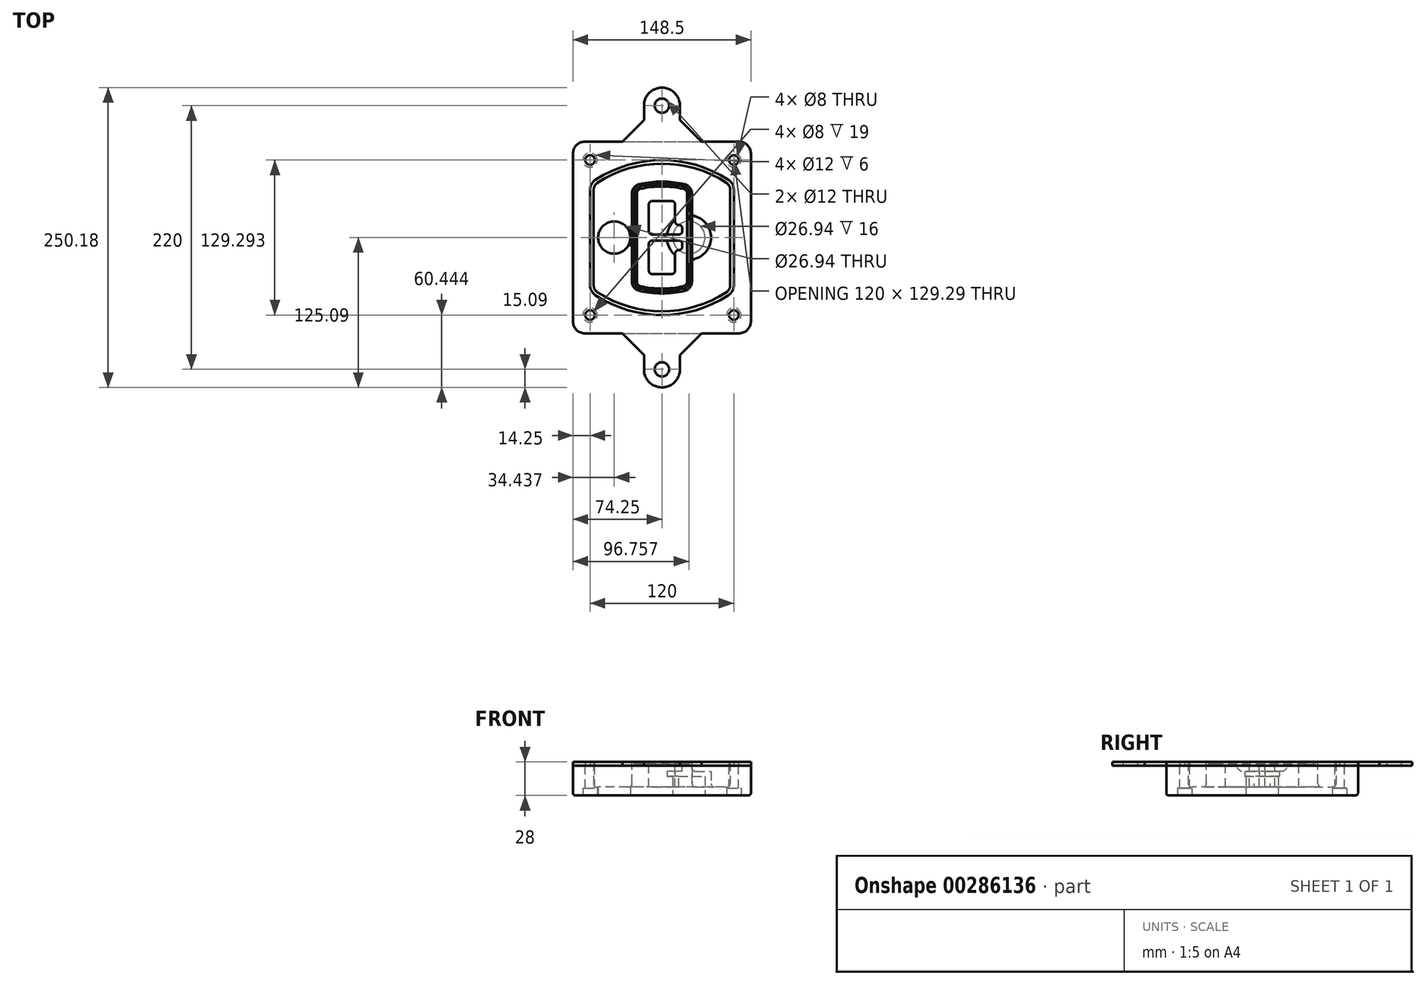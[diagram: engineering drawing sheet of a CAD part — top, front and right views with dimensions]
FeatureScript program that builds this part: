
annotation { "Feature Type Name" : "Feature", "Feature Type Description" : "" }
export const myFeature = defineFeature(function(context is Context, id is Id, definition is map)
    precondition{}
    {
        {
            var Q0;
            Q0=qCreatedBy(makeId("Top.planeOp"),FACE);
            var sketch = newSketch(context, id + "F0", { "sketchPlane" : qUnion([Q0])});
            skPoint(sketch, "E0.rect.middle", {"position": v(0, 0) * mm});
            skLineSegment(sketch, "E1.bottom", {"start": v(-64.25, -80) * mm, "end": v(64.25, -80) * mm});
            skLineSegment(sketch, "E1.top", {"start": v(-64.25, 80) * mm, "end": v(64.25, 80) * mm});
            skLineSegment(sketch, "E1.left", {"start": v(-74.25, -70) * mm, "end": v(-74.25, 70) * mm});
            skLineSegment(sketch, "E1.right", {"start": v(74.25, -70) * mm, "end": v(74.25, 70) * mm});
            skLineSegment(sketch, "E2", {"start": v(-74.25, 80) * mm, "end": v(74.25, -80) * mm, "construction": true});
            skLineSegment(sketch, "E3", {"start": v(74.25, 80) * mm, "end": v(-74.25, -80) * mm, "construction": true});
            skCircle(sketch, "E4", {"center": v(-60, 64.65) * mm, "radius": 4 * mm});
            skCircle(sketch, "E5", {"center": v(60, 64.65) * mm, "radius": 4 * mm});
            skCircle(sketch, "E6", {"center": v(60, -64.65) * mm, "radius": 4 * mm});
            skCircle(sketch, "E7", {"center": v(-60, -64.65) * mm, "radius": 4 * mm});
            skLineSegment(sketch, "E8", {"start": v(-60, 64.65) * mm, "end": v(60, 64.65) * mm, "construction": true});
            skLineSegment(sketch, "E9", {"start": v(60, 64.65) * mm, "end": v(60, -64.65) * mm, "construction": true});
            skLineSegment(sketch, "E10", {"start": v(60, -64.65) * mm, "end": v(-60, -64.65) * mm, "construction": true});
            skLineSegment(sketch, "E11", {"start": v(-60, -64.65) * mm, "end": v(-60, 64.65) * mm, "construction": true});
            skLineSegment(sketch, "E12", {"start": v(-60, 39.77) * mm, "end": v(-60, -39.77) * mm});
            skLineSegment(sketch, "E13", {"start": v(60, 39.77) * mm, "end": v(60, -39.77) * mm});
            skArc(sketch, "E14", {"start": v(55.47, 48.14) * mm, "mid": v(0, 64.65) * mm, "end": v(-55.47, 48.14) * mm});
            skArc(sketch, "E15", {"start": v(-55.47, -48.14) * mm, "mid": v(0, -64.65) * mm, "end": v(55.47, -48.14) * mm});
            skLineSegment(sketch, "E16", {"start": v(-60, 0) * mm, "end": v(60, 0) * mm, "construction": true});
            skPoint(sketch, "E17.visualSharp", {"position": v(-60, -45) * mm});
            skArc(sketch, "E17.filletArc", {"start": v(-60, -39.77) * mm, "mid": v(-58.8, -44.53) * mm, "end": v(-55.47, -48.14) * mm});
            skPoint(sketch, "E18.visualSharp", {"position": v(-60, 45) * mm});
            skArc(sketch, "E18.filletArc", {"start": v(-55.47, 48.14) * mm, "mid": v(-58.8, 44.53) * mm, "end": v(-60, 39.77) * mm});
            skPoint(sketch, "E19.visualSharp", {"position": v(60, 45) * mm});
            skArc(sketch, "E19.filletArc", {"start": v(60, 39.77) * mm, "mid": v(58.8, 44.53) * mm, "end": v(55.47, 48.14) * mm});
            skPoint(sketch, "E20.visualSharp", {"position": v(60, -45) * mm});
            skArc(sketch, "E20.filletArc", {"start": v(55.47, -48.14) * mm, "mid": v(58.8, -44.53) * mm, "end": v(60, -39.77) * mm});
            skPoint(sketch, "E21.visualSharp", {"position": v(-74.25, 80) * mm});
            skArc(sketch, "E21.filletArc", {"start": v(-64.25, 80) * mm, "mid": v(-71.32, 77.07) * mm, "end": v(-74.25, 70) * mm});
            skPoint(sketch, "E22.visualSharp", {"position": v(74.25, 80) * mm});
            skArc(sketch, "E22.filletArc", {"start": v(74.25, 70) * mm, "mid": v(71.32, 77.07) * mm, "end": v(64.25, 80) * mm});
            skPoint(sketch, "E23.visualSharp", {"position": v(74.25, -80) * mm});
            skArc(sketch, "E23.filletArc", {"start": v(64.25, -80) * mm, "mid": v(71.32, -77.07) * mm, "end": v(74.25, -70) * mm});
            skPoint(sketch, "E24.visualSharp", {"position": v(-74.25, -80) * mm});
            skArc(sketch, "E24.filletArc", {"start": v(-74.25, -70) * mm, "mid": v(-71.32, -77.07) * mm, "end": v(-64.25, -80) * mm});
            skArc(sketch, "E25.0", {"start": v(57, 39.77) * mm, "mid": v(56.16, 43.1) * mm, "end": v(53.83, 45.63) * mm});
            skLineSegment(sketch, "E25.1", {"start": v(57, 39.77) * mm, "end": v(57, -39.77) * mm});
            skArc(sketch, "E25.2", {"start": v(53.83, -45.63) * mm, "mid": v(56.16, -43.1) * mm, "end": v(57, -39.77) * mm});
            skArc(sketch, "E25.3", {"start": v(-53.83, -45.63) * mm, "mid": v(0, -61.65) * mm, "end": v(53.83, -45.63) * mm});
            skArc(sketch, "E25.4", {"start": v(-57, -39.77) * mm, "mid": v(-56.16, -43.1) * mm, "end": v(-53.83, -45.63) * mm});
            skArc(sketch, "E25.5", {"start": v(53.83, 45.63) * mm, "mid": v(0, 61.65) * mm, "end": v(-53.83, 45.63) * mm});
            skLineSegment(sketch, "E25.6", {"start": v(-57, 39.77) * mm, "end": v(-57, -39.77) * mm});
            skArc(sketch, "E25.7", {"start": v(-53.83, 45.63) * mm, "mid": v(-56.16, 43.1) * mm, "end": v(-57, 39.77) * mm});
            skArc(sketch, "E26.0", {"start": v(-57.66, 51.49) * mm, "mid": v(-62.31, 46.43) * mm, "end": v(-64, 39.77) * mm});
            skArc(sketch, "E26.1", {"start": v(57.66, 51.49) * mm, "mid": v(0, 68.65) * mm, "end": v(-57.66, 51.49) * mm});
            skArc(sketch, "E26.2", {"start": v(64, 39.77) * mm, "mid": v(62.31, 46.43) * mm, "end": v(57.66, 51.49) * mm});
            skLineSegment(sketch, "E26.3", {"start": v(64, 39.77) * mm, "end": v(64, -39.77) * mm});
            skArc(sketch, "E26.4", {"start": v(57.66, -51.49) * mm, "mid": v(62.31, -46.43) * mm, "end": v(64, -39.77) * mm});
            skLineSegment(sketch, "E26.5", {"start": v(-64, 39.77) * mm, "end": v(-64, -39.77) * mm});
            skArc(sketch, "E26.6", {"start": v(-57.66, -51.49) * mm, "mid": v(0, -68.65) * mm, "end": v(57.66, -51.49) * mm});
            skArc(sketch, "E26.7", {"start": v(-64, -39.77) * mm, "mid": v(-62.31, -46.43) * mm, "end": v(-57.66, -51.49) * mm});
            skSolve(sketch);
        }
        {
            var Q0;
            Q0=makeQuery(id+"F0.imprint","IMPRINT",FACE,{"disambiguationData":[TD([[makeQuery(id+"F0.imprint","IMPRINT",EDGE,{"derivedFrom":sQuery(id+"F0.wireOp",EDGE,"E1.bottom")}),1.0]])]});
            var Q1;
            Q1=makeQuery(id+"F0.imprint","IMPRINT",FACE,{"disambiguationData":[TD([[makeQuery(id+"F0.imprint","IMPRINT",EDGE,{"derivedFrom":sQuery(id+"F0.wireOp",EDGE,"E12")}),1.0]])]});
            var Q2;
            Q2=makeQuery(id+"F0.imprint","IMPRINT",FACE,{"disambiguationData":[TD([[makeQuery(id+"F0.imprint","IMPRINT",EDGE,{"derivedFrom":sQuery(id+"F0.wireOp",EDGE,"E25.0")}),1.0]])]});
            var Q3;
            Q3=makeQuery(id+"F0.imprint","IMPRINT",FACE,{"disambiguationData":[TD([[makeQuery(id+"F0.imprint","IMPRINT",EDGE,{"derivedFrom":sQuery(id+"F0.wireOp",EDGE,"E12")}),-1.0]])]});
            extrude(context, id + "F1", {"entities" : qUnion([Q0, Q1, Q2, Q3]), "oppositeDirection" : true, "depth" : 25 * mm});
        }
        {
            var Q0;
            Q0=makeQuery(id+"F0.imprint","IMPRINT",FACE,{"disambiguationData":[TD([[makeQuery(id+"F0.imprint","IMPRINT",EDGE,{"derivedFrom":sQuery(id+"F0.wireOp",EDGE,"E12")}),1.0]])]});
            extrude(context, id + "F2", {"entities" : qUnion([Q0]), "operationType" : NewBodyOperationType.ADD, "depth" : 3 * mm});
        }
        {
            var Q0;
            Q0=makeQuery(id+"F0.imprint","IMPRINT",FACE,{"disambiguationData":[TD([[makeQuery(id+"F0.imprint","IMPRINT",EDGE,{"derivedFrom":sQuery(id+"F0.wireOp",EDGE,"E25.0")}),1.0]])]});
            extrude(context, id + "F3", {"entities" : qUnion([Q0]), "operationType" : NewBodyOperationType.REMOVE, "oppositeDirection" : true, "depth" : 18 * mm});
        }
        {
            var Q0;
            Q0=makeQuery(id+"F2.opExtrude","CAP_FACE",FACE,{"disambiguationData":[OSD([sQuery(id+"F0.wireOp",EDGE,"E12"),sQuery(id+"F0.wireOp",EDGE,"E13"),sQuery(id+"F0.wireOp",EDGE,"E14"),sQuery(id+"F0.wireOp",EDGE,"E15"),sQuery(id+"F0.wireOp",EDGE,"E17.filletArc"),sQuery(id+"F0.wireOp",EDGE,"E18.filletArc"),sQuery(id+"F0.wireOp",EDGE,"E19.filletArc"),sQuery(id+"F0.wireOp",EDGE,"E20.filletArc"),sQuery(id+"F0.wireOp",EDGE,"E25.0"),sQuery(id+"F0.wireOp",EDGE,"E25.1"),sQuery(id+"F0.wireOp",EDGE,"E25.2"),sQuery(id+"F0.wireOp",EDGE,"E25.3"),sQuery(id+"F0.wireOp",EDGE,"E25.4"),sQuery(id+"F0.wireOp",EDGE,"E25.5"),sQuery(id+"F0.wireOp",EDGE,"E25.6"),sQuery(id+"F0.wireOp",EDGE,"E25.7")])],"isStart":false});
            var sketch = newSketch(context, id + "F4", { "sketchPlane" : qUnion([Q0])});
            skArc(sketch, "E27.0", {"start": v(-18.8, -44.5) * mm, "mid": v(0, -46.65) * mm, "end": v(18.8, -44.5) * mm});
            skArc(sketch, "E28.0", {"start": v(18.8, 44.5) * mm, "mid": v(0, 46.65) * mm, "end": v(-18.8, 44.5) * mm});
            skLineSegment(sketch, "E29", {"start": v(-25, 36.7) * mm, "end": v(-25, -36.7) * mm});
            skLineSegment(sketch, "E30", {"start": v(25, 36.7) * mm, "end": v(25, -36.7) * mm});
            skLineSegment(sketch, "E31", {"start": v(-25, 42.81) * mm, "end": v(25, 42.81) * mm, "construction": true});
            skLineSegment(sketch, "E32", {"start": v(-25, -42.81) * mm, "end": v(25, -42.81) * mm, "construction": true});
            skPoint(sketch, "E33.visualSharp", {"position": v(-25, 42.81) * mm});
            skArc(sketch, "E33.filletArc", {"start": v(-18.8, 44.5) * mm, "mid": v(-23.26, 41.69) * mm, "end": v(-25, 36.7) * mm});
            skPoint(sketch, "E34.visualSharp", {"position": v(25, 42.81) * mm});
            skArc(sketch, "E34.filletArc", {"start": v(25, 36.7) * mm, "mid": v(23.26, 41.69) * mm, "end": v(18.8, 44.5) * mm});
            skPoint(sketch, "E35.visualSharp", {"position": v(25, -42.81) * mm});
            skArc(sketch, "E35.filletArc", {"start": v(18.8, -44.5) * mm, "mid": v(23.26, -41.69) * mm, "end": v(25, -36.7) * mm});
            skPoint(sketch, "E36.visualSharp", {"position": v(-25, -42.81) * mm});
            skArc(sketch, "E36.filletArc", {"start": v(-25, -36.7) * mm, "mid": v(-23.26, -41.69) * mm, "end": v(-18.8, -44.5) * mm});
            skArc(sketch, "E37.0", {"start": v(53.83, 45.63) * mm, "mid": v(0, 61.65) * mm, "end": v(-53.83, 45.63) * mm});
            skArc(sketch, "E37.1", {"start": v(-53.83, 45.63) * mm, "mid": v(-56.16, 43.1) * mm, "end": v(-57, 39.77) * mm});
            skLineSegment(sketch, "E37.2", {"start": v(-57, 39.77) * mm, "end": v(-57, -39.77) * mm});
            skArc(sketch, "E37.3", {"start": v(-57, -39.77) * mm, "mid": v(-56.16, -43.1) * mm, "end": v(-53.83, -45.63) * mm});
            skArc(sketch, "E37.4", {"start": v(-53.83, -45.63) * mm, "mid": v(0, -61.65) * mm, "end": v(53.83, -45.63) * mm});
            skArc(sketch, "E37.5", {"start": v(53.83, -45.63) * mm, "mid": v(56.16, -43.1) * mm, "end": v(57, -39.77) * mm});
            skLineSegment(sketch, "E37.6", {"start": v(57, 39.77) * mm, "end": v(57, -39.77) * mm});
            skArc(sketch, "E37.7", {"start": v(57, 39.77) * mm, "mid": v(56.16, 43.1) * mm, "end": v(53.83, 45.63) * mm});
            skLineSegment(sketch, "E38.0", {"start": v(23, 36.7) * mm, "end": v(23, -36.7) * mm});
            skArc(sketch, "E38.1", {"start": v(18.35, -42.55) * mm, "mid": v(21.7, -40.44) * mm, "end": v(23, -36.7) * mm});
            skArc(sketch, "E38.2", {"start": v(-18.35, -42.55) * mm, "mid": v(0, -44.65) * mm, "end": v(18.35, -42.55) * mm});
            skArc(sketch, "E38.3", {"start": v(-23, -36.7) * mm, "mid": v(-21.7, -40.44) * mm, "end": v(-18.35, -42.55) * mm});
            skLineSegment(sketch, "E38.4", {"start": v(-23, 36.7) * mm, "end": v(-23, -36.7) * mm});
            skArc(sketch, "E38.5", {"start": v(23, 36.7) * mm, "mid": v(21.7, 40.44) * mm, "end": v(18.35, 42.55) * mm});
            skArc(sketch, "E38.6", {"start": v(-18.35, 42.55) * mm, "mid": v(-21.7, 40.44) * mm, "end": v(-23, 36.7) * mm});
            skArc(sketch, "E38.7", {"start": v(18.35, 42.55) * mm, "mid": v(0, 44.65) * mm, "end": v(-18.35, 42.55) * mm});
            skArc(sketch, "E39.0", {"start": v(21, 36.7) * mm, "mid": v(20.13, 39.2) * mm, "end": v(17.9, 40.6) * mm});
            skLineSegment(sketch, "E39.1", {"start": v(21, 36.7) * mm, "end": v(21, -36.7) * mm});
            skArc(sketch, "E39.2", {"start": v(17.9, -40.6) * mm, "mid": v(20.13, -39.2) * mm, "end": v(21, -36.7) * mm});
            skArc(sketch, "E39.3", {"start": v(-17.9, -40.6) * mm, "mid": v(0, -42.65) * mm, "end": v(17.9, -40.6) * mm});
            skArc(sketch, "E39.4", {"start": v(-21, -36.7) * mm, "mid": v(-20.13, -39.2) * mm, "end": v(-17.9, -40.6) * mm});
            skArc(sketch, "E39.5", {"start": v(17.9, 40.6) * mm, "mid": v(0, 42.65) * mm, "end": v(-17.9, 40.6) * mm});
            skLineSegment(sketch, "E39.6", {"start": v(-21, 36.7) * mm, "end": v(-21, -36.7) * mm});
            skArc(sketch, "E39.7", {"start": v(-17.9, 40.6) * mm, "mid": v(-20.13, 39.2) * mm, "end": v(-21, 36.7) * mm});
            skLineSegment(sketch, "E40", {"start": v(-25, 0) * mm, "end": v(25, 0) * mm, "construction": true});
            skLineSegment(sketch, "E41", {"start": v(-11, 5.5) * mm, "end": v(-11, 27.5) * mm});
            skLineSegment(sketch, "E42", {"start": v(-8, 30.5) * mm, "end": v(8, 30.5) * mm});
            skLineSegment(sketch, "E43", {"start": v(11, 27.5) * mm, "end": v(11, 13.5) * mm});
            skLineSegment(sketch, "E44", {"start": v(14, 10.5) * mm, "end": v(14, 10.5) * mm});
            skLineSegment(sketch, "E45", {"start": v(17, 7.5) * mm, "end": v(17, 5.5) * mm});
            skLineSegment(sketch, "E46", {"start": v(14, 2.5) * mm, "end": v(-8, 2.5) * mm});
            skPoint(sketch, "E47.visualSharp", {"position": v(-11, 30.5) * mm});
            skArc(sketch, "E47.filletArc", {"start": v(-8, 30.5) * mm, "mid": v(-10.12, 29.62) * mm, "end": v(-11, 27.5) * mm});
            skPoint(sketch, "E48.visualSharp", {"position": v(11, 30.5) * mm});
            skArc(sketch, "E48.filletArc", {"start": v(11, 27.5) * mm, "mid": v(10.12, 29.62) * mm, "end": v(8, 30.5) * mm});
            skPoint(sketch, "E49.visualSharp", {"position": v(11, 10.5) * mm});
            skArc(sketch, "E49.filletArc", {"start": v(11, 13.5) * mm, "mid": v(11.88, 11.38) * mm, "end": v(14, 10.5) * mm});
            skPoint(sketch, "E50.visualSharp", {"position": v(17, 10.5) * mm});
            skArc(sketch, "E50.filletArc", {"start": v(17, 7.5) * mm, "mid": v(16.12, 9.62) * mm, "end": v(14, 10.5) * mm});
            skPoint(sketch, "E51.visualSharp", {"position": v(17, 2.5) * mm});
            skArc(sketch, "E51.filletArc", {"start": v(14, 2.5) * mm, "mid": v(16.12, 3.38) * mm, "end": v(17, 5.5) * mm});
            skPoint(sketch, "E52.visualSharp", {"position": v(-11, 2.5) * mm});
            skArc(sketch, "E52.filletArc", {"start": v(-11, 5.5) * mm, "mid": v(-10.12, 3.38) * mm, "end": v(-8, 2.5) * mm});
            skLineSegment(sketch, "E53.0.MirrorCS", {"start": v(14, -2.5) * mm, "end": v(-8, -2.5) * mm});
            skArc(sketch, "E54.0.MirrorCS", {"start": v(-11, -5.5) * mm, "mid": v(-10.12, -3.38) * mm, "end": v(-8, -2.5) * mm});
            skLineSegment(sketch, "E55.0.MirrorCS", {"start": v(-11, -5.5) * mm, "end": v(-11, -27.5) * mm});
            skArc(sketch, "E56.0.MirrorCS", {"start": v(-8, -30.5) * mm, "mid": v(-10.12, -29.62) * mm, "end": v(-11, -27.5) * mm});
            skLineSegment(sketch, "E57.0.MirrorCS", {"start": v(-8, -30.5) * mm, "end": v(8, -30.5) * mm});
            skArc(sketch, "E58.0.MirrorCS", {"start": v(11, -27.5) * mm, "mid": v(10.12, -29.62) * mm, "end": v(8, -30.5) * mm});
            skLineSegment(sketch, "E59.0.MirrorCS", {"start": v(11, -27.5) * mm, "end": v(11, -13.5) * mm});
            skArc(sketch, "E60.0.MirrorCS", {"start": v(11, -13.5) * mm, "mid": v(11.88, -11.38) * mm, "end": v(14, -10.5) * mm});
            skArc(sketch, "E61.0.MirrorCS", {"start": v(17, -7.5) * mm, "mid": v(16.12, -9.62) * mm, "end": v(14, -10.5) * mm});
            skLineSegment(sketch, "E62.0.MirrorCS", {"start": v(17, -7.5) * mm, "end": v(17, -5.5) * mm});
            skArc(sketch, "E63.0.MirrorCS", {"start": v(14, -2.5) * mm, "mid": v(16.12, -3.38) * mm, "end": v(17, -5.5) * mm});
            skSolve(sketch);
        }
        {
            var Q0;
            Q0=makeQuery(id+"F4.imprint","IMPRINT",FACE,{"disambiguationData":[TD([[makeQuery(id+"F4.imprint","IMPRINT",EDGE,{"derivedFrom":sQuery(id+"F4.wireOp",EDGE,"E27.0")}),1.0]])]});
            var Q1;
            Q1=makeQuery(id+"F4.imprint","IMPRINT",FACE,{"disambiguationData":[TD([[makeQuery(id+"F4.imprint","IMPRINT",EDGE,{"derivedFrom":sQuery(id+"F4.wireOp",EDGE,"E38.0")}),-1.0]])]});
            var Q2;
            Q2=makeQuery(id+"F4.imprint","IMPRINT",FACE,{"disambiguationData":[TD([[makeQuery(id+"F4.imprint","IMPRINT",EDGE,{"derivedFrom":sQuery(id+"F4.wireOp",EDGE,"E39.0")}),1.0]])]});
            extrude(context, id + "F5", {"entities" : qUnion([Q0, Q1, Q2]), "operationType" : NewBodyOperationType.ADD, "endBound" : BoundingType.UP_TO_NEXT, "oppositeDirection" : true, "depth" : 25 * mm});
        }
        {
            var Q0;
            Q0=makeQuery(id+"F4.imprint","IMPRINT",FACE,{"disambiguationData":[TD([[makeQuery(id+"F4.imprint","IMPRINT",EDGE,{"derivedFrom":sQuery(id+"F4.wireOp",EDGE,"E38.0")}),-1.0]])]});
            extrude(context, id + "F6", {"entities" : qUnion([Q0]), "operationType" : NewBodyOperationType.REMOVE, "oppositeDirection" : true, "depth" : 2 * mm});
        }
        {
            var Q0;
            Q0=makeQuery(id+"F1.opExtrude","CAP_FACE",FACE,{"disambiguationData":[OSD([sQuery(id+"F0.wireOp",EDGE,"E1.bottom"),sQuery(id+"F0.wireOp",EDGE,"E1.top"),sQuery(id+"F0.wireOp",EDGE,"E1.left"),sQuery(id+"F0.wireOp",EDGE,"E1.right"),sQuery(id+"F0.wireOp",EDGE,"E4"),sQuery(id+"F0.wireOp",EDGE,"E5"),sQuery(id+"F0.wireOp",EDGE,"E6"),sQuery(id+"F0.wireOp",EDGE,"E7"),sQuery(id+"F0.wireOp",EDGE,"E21.filletArc"),sQuery(id+"F0.wireOp",EDGE,"E22.filletArc"),sQuery(id+"F0.wireOp",EDGE,"E23.filletArc"),sQuery(id+"F0.wireOp",EDGE,"E24.filletArc")])],"isStart":false});
            var sketch = newSketch(context, id + "F7", { "sketchPlane" : qUnion([Q0])});
            skCircle(sketch, "E64", {"center": v(22.5, 0) * mm, "radius": 13.47 * mm});
            skCircle(sketch, "E65", {"center": v(-39.81, 0) * mm, "radius": 13.47 * mm});
            skLineSegment(sketch, "E66", {"start": v(74.25, 0) * mm, "end": v(-74.25, 0) * mm});
            skCircle(sketch, "E67", {"center": v(22.5, 0) * mm, "radius": 18.47 * mm});
            skCircle(sketch, "E68", {"center": v(60, -64.65) * mm, "radius": 6 * mm});
            skCircle(sketch, "E69", {"center": v(-60, -64.65) * mm, "radius": 6 * mm});
            skCircle(sketch, "E70", {"center": v(-60, 64.65) * mm, "radius": 6 * mm});
            skCircle(sketch, "E71", {"center": v(60, 64.65) * mm, "radius": 6 * mm});
            skSolve(sketch);
        }
        {
            var Q0;
            {var subQ1=sQuery(id+"F7.wireOp",EDGE,"E66");var subQ4=sQuery(id+"F7.wireOp",EDGE,"E64");var subQ6=makeQuery(id+"F7.imprint","INTERSECT",VERTEX,{"disambiguationData":[OD(0.0)],"derivedFrom":[subQ4,subQ1]});Q0=makeQuery(id+"F7.imprint","IMPRINT",FACE,{"disambiguationData":[TD([[makeQuery(id+"F7.imprint","IMPRINT",EDGE,{"disambiguationData":[TD([[subQ6,-1.0]])],"derivedFrom":subQ4}),-1.0]])]});}
            var Q1;
            {var subQ0=sQuery(id+"F7.wireOp",EDGE,"E66");var subQ1=sQuery(id+"F7.wireOp",EDGE,"E64");var subQ3=makeQuery(id+"F7.imprint","INTERSECT",VERTEX,{"disambiguationData":[OD(0.0)],"derivedFrom":[subQ1,subQ0]});Q1=makeQuery(id+"F7.imprint","IMPRINT",FACE,{"disambiguationData":[TD([[makeQuery(id+"F7.imprint","IMPRINT",EDGE,{"disambiguationData":[TD([[subQ3,-1.0]])],"derivedFrom":subQ1}),1.0]])]});}
            var Q2;
            {var subQ0=sQuery(id+"F7.wireOp",EDGE,"E66");var subQ1=sQuery(id+"F7.wireOp",EDGE,"E64");var subQ3=makeQuery(id+"F7.imprint","INTERSECT",VERTEX,{"disambiguationData":[OD(0.0)],"derivedFrom":[subQ1,subQ0]});Q2=makeQuery(id+"F7.imprint","IMPRINT",FACE,{"disambiguationData":[TD([[makeQuery(id+"F7.imprint","IMPRINT",EDGE,{"disambiguationData":[TD([[subQ3,1.0]])],"derivedFrom":subQ1}),1.0]])]});}
            var Q3;
            {var subQ1=sQuery(id+"F7.wireOp",EDGE,"E66");var subQ4=sQuery(id+"F7.wireOp",EDGE,"E64");var subQ6=makeQuery(id+"F7.imprint","INTERSECT",VERTEX,{"disambiguationData":[OD(0.0)],"derivedFrom":[subQ4,subQ1]});Q3=makeQuery(id+"F7.imprint","IMPRINT",FACE,{"disambiguationData":[TD([[makeQuery(id+"F7.imprint","IMPRINT",EDGE,{"disambiguationData":[TD([[subQ6,1.0]])],"derivedFrom":subQ4}),-1.0]])]});}
            extrude(context, id + "F8", {"entities" : qUnion([Q0, Q1, Q2, Q3]), "operationType" : NewBodyOperationType.ADD, "oppositeDirection" : true, "depth" : 20 * mm});
        }
        {
            var Q0;
            {var subQ0=sQuery(id+"F7.wireOp",EDGE,"E66");var subQ1=sQuery(id+"F7.wireOp",EDGE,"E64");var subQ3=makeQuery(id+"F7.imprint","INTERSECT",VERTEX,{"disambiguationData":[OD(0.0)],"derivedFrom":[subQ1,subQ0]});Q0=makeQuery(id+"F7.imprint","IMPRINT",FACE,{"disambiguationData":[TD([[makeQuery(id+"F7.imprint","IMPRINT",EDGE,{"disambiguationData":[TD([[subQ3,-1.0]])],"derivedFrom":subQ1}),1.0]])]});}
            var Q1;
            {var subQ0=sQuery(id+"F7.wireOp",EDGE,"E66");var subQ1=sQuery(id+"F7.wireOp",EDGE,"E64");var subQ3=makeQuery(id+"F7.imprint","INTERSECT",VERTEX,{"disambiguationData":[OD(0.0)],"derivedFrom":[subQ1,subQ0]});Q1=makeQuery(id+"F7.imprint","IMPRINT",FACE,{"disambiguationData":[TD([[makeQuery(id+"F7.imprint","IMPRINT",EDGE,{"disambiguationData":[TD([[subQ3,1.0]])],"derivedFrom":subQ1}),1.0]])]});}
            extrude(context, id + "F9", {"entities" : qUnion([Q0, Q1]), "operationType" : NewBodyOperationType.REMOVE, "oppositeDirection" : true, "depth" : 16 * mm});
        }
        {
            var Q0;
            {var subQ0=sQuery(id+"F7.wireOp",EDGE,"E66");var subQ1=sQuery(id+"F7.wireOp",EDGE,"E65");var subQ3=makeQuery(id+"F7.imprint","INTERSECT",VERTEX,{"disambiguationData":[OD(0.0)],"derivedFrom":[subQ1,subQ0]});Q0=makeQuery(id+"F7.imprint","IMPRINT",FACE,{"disambiguationData":[TD([[makeQuery(id+"F7.imprint","IMPRINT",EDGE,{"disambiguationData":[TD([[subQ3,-1.0]])],"derivedFrom":subQ1}),1.0]])]});}
            var Q1;
            {var subQ0=sQuery(id+"F7.wireOp",EDGE,"E66");var subQ1=sQuery(id+"F7.wireOp",EDGE,"E65");var subQ3=makeQuery(id+"F7.imprint","INTERSECT",VERTEX,{"disambiguationData":[OD(0.0)],"derivedFrom":[subQ1,subQ0]});Q1=makeQuery(id+"F7.imprint","IMPRINT",FACE,{"disambiguationData":[TD([[makeQuery(id+"F7.imprint","IMPRINT",EDGE,{"disambiguationData":[TD([[subQ3,1.0]])],"derivedFrom":subQ1}),1.0]])]});}
            extrude(context, id + "F10", {"entities" : qUnion([Q0, Q1]), "operationType" : NewBodyOperationType.REMOVE, "oppositeDirection" : true, "depth" : 25 * mm});
        }
        {
            var Q0;
            Q0=makeQuery(id+"F7.imprint","IMPRINT",FACE,{"disambiguationData":[TD([[makeQuery(id+"F7.imprint","IMPRINT",EDGE,{"derivedFrom":sQuery(id+"F7.wireOp",EDGE,"E68")}),1.0]])]});
            var Q1;
            Q1=makeQuery(id+"F7.imprint","IMPRINT",FACE,{"disambiguationData":[TD([[makeQuery(id+"F7.imprint","IMPRINT",EDGE,{"derivedFrom":makeQuery(id+"F1.opExtrude","CAP_EDGE",EDGE,{"disambiguationData":[OSD([sQuery(id+"F0.wireOp",EDGE,"E5")])],"isStart":false})}),-1.0]])]});
            var Q2;
            Q2=makeQuery(id+"F7.imprint","IMPRINT",FACE,{"disambiguationData":[TD([[makeQuery(id+"F7.imprint","IMPRINT",EDGE,{"derivedFrom":sQuery(id+"F7.wireOp",EDGE,"E69")}),1.0]])]});
            var Q3;
            Q3=makeQuery(id+"F7.imprint","IMPRINT",FACE,{"disambiguationData":[TD([[makeQuery(id+"F7.imprint","IMPRINT",EDGE,{"derivedFrom":makeQuery(id+"F1.opExtrude","CAP_EDGE",EDGE,{"disambiguationData":[OSD([sQuery(id+"F0.wireOp",EDGE,"E4")])],"isStart":false})}),-1.0]])]});
            var Q4;
            Q4=makeQuery(id+"F7.imprint","IMPRINT",FACE,{"disambiguationData":[TD([[makeQuery(id+"F7.imprint","IMPRINT",EDGE,{"derivedFrom":sQuery(id+"F7.wireOp",EDGE,"E70")}),1.0]])]});
            var Q5;
            Q5=makeQuery(id+"F7.imprint","IMPRINT",FACE,{"disambiguationData":[TD([[makeQuery(id+"F7.imprint","IMPRINT",EDGE,{"derivedFrom":makeQuery(id+"F1.opExtrude","CAP_EDGE",EDGE,{"disambiguationData":[OSD([sQuery(id+"F0.wireOp",EDGE,"E7")])],"isStart":false})}),-1.0]])]});
            var Q6;
            Q6=makeQuery(id+"F7.imprint","IMPRINT",FACE,{"disambiguationData":[TD([[makeQuery(id+"F7.imprint","IMPRINT",EDGE,{"derivedFrom":sQuery(id+"F7.wireOp",EDGE,"E71")}),1.0]])]});
            var Q7;
            Q7=makeQuery(id+"F7.imprint","IMPRINT",FACE,{"disambiguationData":[TD([[makeQuery(id+"F7.imprint","IMPRINT",EDGE,{"derivedFrom":makeQuery(id+"F1.opExtrude","CAP_EDGE",EDGE,{"disambiguationData":[OSD([sQuery(id+"F0.wireOp",EDGE,"E6")])],"isStart":false})}),-1.0]])]});
            extrude(context, id + "F11", {"entities" : qUnion([Q0, Q1, Q2, Q3, Q4, Q5, Q6, Q7]), "operationType" : NewBodyOperationType.REMOVE, "oppositeDirection" : true, "depth" : 6 * mm});
        }
        {
            var Q0;
            Q0=makeQuery(id+"F9.boolean.opBoolean","COPY",FACE,{"derivedFrom":makeQuery(id+"F9.opExtrude","CAP_FACE",FACE,{"disambiguationData":[OSD([sQuery(id+"F7.wireOp",EDGE,"E64")])],"isStart":false})});
            var sketch = newSketch(context, id + "F12", { "sketchPlane" : qUnion([Q0])});
            skArc(sketch, "E72.0", {"start": v(11, 14.45) * mm, "mid": v(6.45, 9.13) * mm, "end": v(4.2, 2.5) * mm});
            skArc(sketch, "E72.1", {"start": v(4.2, -2.5) * mm, "mid": v(6.45, -9.13) * mm, "end": v(11, -14.45) * mm});
            skLineSegment(sketch, "E73", {"start": v(4.2, -2.5) * mm, "end": v(14, -2.5) * mm});
            skLineSegment(sketch, "E74.0", {"start": v(14, 2.5) * mm, "end": v(4.2, 2.5) * mm});
            skArc(sketch, "E74.1", {"start": v(14, 2.5) * mm, "mid": v(16.12, 3.38) * mm, "end": v(17, 5.5) * mm});
            skLineSegment(sketch, "E74.2", {"start": v(17, 7.5) * mm, "end": v(17, 5.5) * mm});
            skArc(sketch, "E74.3", {"start": v(17, 7.5) * mm, "mid": v(16.12, 9.62) * mm, "end": v(14, 10.5) * mm});
            skArc(sketch, "E74.4", {"start": v(11, 13.5) * mm, "mid": v(11.88, 11.38) * mm, "end": v(14, 10.5) * mm});
            skLineSegment(sketch, "E74.5", {"start": v(11, 14.45) * mm, "end": v(11, 13.5) * mm});
            skLineSegment(sketch, "E74.7", {"start": v(14, -2.5) * mm, "end": v(4.2, -2.5) * mm});
            skArc(sketch, "E74.8", {"start": v(14, -2.5) * mm, "mid": v(16.12, -3.38) * mm, "end": v(17, -5.5) * mm});
            skLineSegment(sketch, "E74.9", {"start": v(17, -7.5) * mm, "end": v(17, -5.5) * mm});
            skArc(sketch, "E74.10", {"start": v(17, -7.5) * mm, "mid": v(16.12, -9.62) * mm, "end": v(14, -10.5) * mm});
            skArc(sketch, "E74.11", {"start": v(11, -13.5) * mm, "mid": v(11.88, -11.38) * mm, "end": v(14, -10.5) * mm});
            skLineSegment(sketch, "E74.12", {"start": v(11, -14.45) * mm, "end": v(11, -13.5) * mm});
            skPoint(sketch, "E75.orphan", {"position": v(11, -27.5) * mm});
            skPoint(sketch, "E76.orphan", {"position": v(-8, -2.5) * mm});
            skPoint(sketch, "E77.orphan", {"position": v(-8, 2.5) * mm});
            skPoint(sketch, "E78.orphan", {"position": v(11, 27.5) * mm});
            skSolve(sketch);
        }
        {
            var Q0;
            {var subQ7=sQuery(id+"F12.wireOp",EDGE,"E72.0");var subQ14=sQuery(id+"F12.wireOp",EDGE,"E72.1");var subQ16=sQuery(id+"F12.wireOp",EDGE,"E74.1");var subQ18=sQuery(id+"F12.wireOp",EDGE,"E74.8");Q0=qUnion([makeQuery(id+"F12.imprint","IMPRINT",FACE,{"disambiguationData":[TD([[makeQuery(id+"F12.imprint","IMPRINT",EDGE,{"derivedFrom":subQ7}),1.0]])]}),makeQuery(id+"F12.imprint","IMPRINT",FACE,{"disambiguationData":[TD([[makeQuery(id+"F12.imprint","IMPRINT",EDGE,{"derivedFrom":subQ14}),1.0]])]}),makeQuery(id+"F12.imprint","IMPRINT",FACE,{"disambiguationData":[TD([[makeQuery(id+"F12.imprint","IMPRINT",EDGE,{"derivedFrom":subQ16}),1.0]])]}),makeQuery(id+"F12.imprint","IMPRINT",FACE,{"disambiguationData":[TD([[makeQuery(id+"F12.imprint","IMPRINT",EDGE,{"derivedFrom":subQ18}),-1.0]])]})]);}
            var Q1;
            Q1=makeQuery(id+"F5.boolean.opBoolean","SPLIT",FACE,{"disambiguationData":[TD([makeQuery(id+"F5.opExtrude","SWEPT_FACE",FACE,{"disambiguationData":[OSD([sQuery(id+"F4.wireOp",EDGE,"E41")])]})])],"derivedFrom":makeQuery(id+"F3.boolean.opBoolean","COPY",FACE,{"derivedFrom":makeQuery(id+"F3.opExtrude","CAP_FACE",FACE,{"disambiguationData":[OSD([sQuery(id+"F0.wireOp",EDGE,"E25.0"),sQuery(id+"F0.wireOp",EDGE,"E25.1"),sQuery(id+"F0.wireOp",EDGE,"E25.2"),sQuery(id+"F0.wireOp",EDGE,"E25.3"),sQuery(id+"F0.wireOp",EDGE,"E25.4"),sQuery(id+"F0.wireOp",EDGE,"E25.5"),sQuery(id+"F0.wireOp",EDGE,"E25.6"),sQuery(id+"F0.wireOp",EDGE,"E25.7")])],"isStart":false})})});
            extrude(context, id + "F13", {"entities" : qUnion([Q0]), "operationType" : NewBodyOperationType.REMOVE, "endBound" : BoundingType.UP_TO_SURFACE, "endBoundEntityFace" : qUnion([Q1]), "depth" : 25 * mm});
        }
        {
            var Q0;
            Q0=makeQuery(id+"F3.boolean.opBoolean","COPY",EDGE,{"derivedFrom":makeQuery(id+"F3.opExtrude","CAP_EDGE",EDGE,{"disambiguationData":[OSD([sQuery(id+"F0.wireOp",EDGE,"E25.6")])],"isStart":false})});
            var Q1;
            Q1=makeQuery(id+"F8.boolean.opBoolean","INTERSECT",EDGE,{"derivedFrom":[makeQuery(id+"F5.opExtrude","SWEPT_FACE",FACE,{"disambiguationData":[OSD([sQuery(id+"F4.wireOp",EDGE,"E30")])]}),makeQuery(id+"F8.opExtrude","CAP_FACE",FACE,{"disambiguationData":[OSD([sQuery(id+"F7.wireOp",EDGE,"E67")])],"isStart":false})]});
            var Q2;
            Q2=makeQuery(id+"F8.boolean.opBoolean","INTERSECT",EDGE,{"disambiguationData":[OD(1.0)],"derivedFrom":[makeQuery(id+"F5.opExtrude","SWEPT_FACE",FACE,{"disambiguationData":[OSD([sQuery(id+"F4.wireOp",EDGE,"E30")])]}),makeQuery(id+"F8.opExtrude","SWEPT_FACE",FACE,{"disambiguationData":[OSD([sQuery(id+"F7.wireOp",EDGE,"E67")])]})]});
            var Q3;
            {var subQ0=sQuery(id+"F4.wireOp",EDGE,"E30");Q3=makeQuery(id+"F8.boolean.opBoolean","SPLIT",EDGE,{"disambiguationData":[TD([makeQuery(id+"F5.opExtrude","SWEPT_FACE",FACE,{"disambiguationData":[OSD([sQuery(id+"F4.wireOp",EDGE,"E35.filletArc")])]})])],"derivedFrom":makeQuery(id+"F5.opExtrude","CAP_EDGE",EDGE,{"disambiguationData":[OSD([subQ0])],"isStart":false})});}
            var Q4;
            {var subQ0=sQuery(id+"F0.wireOp",EDGE,"E25.7");var subQ1=sQuery(id+"F0.wireOp",EDGE,"E25.1");var subQ2=sQuery(id+"F0.wireOp",EDGE,"E25.6");var subQ3=sQuery(id+"F0.wireOp",EDGE,"E25.5");var subQ4=sQuery(id+"F0.wireOp",EDGE,"E25.4");var subQ5=sQuery(id+"F0.wireOp",EDGE,"E25.0");var subQ6=sQuery(id+"F0.wireOp",EDGE,"E25.2");var subQ7=sQuery(id+"F0.wireOp",EDGE,"E25.3");Q4=makeQuery(id+"F8.boolean.opBoolean","INTERSECT",EDGE,{"derivedFrom":[makeQuery(id+"F5.boolean.opBoolean","SPLIT",FACE,{"disambiguationData":[TD([makeQuery(id+"F2.opExtrude","SWEPT_FACE",FACE,{"disambiguationData":[OSD([subQ5])]})])],"derivedFrom":makeQuery(id+"F3.boolean.opBoolean","COPY",FACE,{"derivedFrom":makeQuery(id+"F3.opExtrude","CAP_FACE",FACE,{"disambiguationData":[OSD([subQ5,subQ1,subQ6,subQ7,subQ4,subQ3,subQ2,subQ0])],"isStart":false})})}),makeQuery(id+"F8.opExtrude","SWEPT_FACE",FACE,{"disambiguationData":[OSD([sQuery(id+"F7.wireOp",EDGE,"E67")])]})]});}
            var Q5;
            Q5=makeQuery(id+"F8.boolean.opBoolean","INTERSECT",EDGE,{"disambiguationData":[OD(0.0)],"derivedFrom":[makeQuery(id+"F5.opExtrude","SWEPT_FACE",FACE,{"disambiguationData":[OSD([sQuery(id+"F4.wireOp",EDGE,"E30")])]}),makeQuery(id+"F8.opExtrude","SWEPT_FACE",FACE,{"disambiguationData":[OSD([sQuery(id+"F7.wireOp",EDGE,"E67")])]})]});
            fillet(context, id + "F14", {"entities" : qUnion([Q0, Q1, Q2, Q3, Q4, Q5]), "radius" : 3 * mm, "tangentPropagation" : true, "allowEdgeOverflow" : false});
        }
        {
            var Q0;
            Q0=makeQuery(id+"F1.opExtrude","CAP_EDGE",EDGE,{"disambiguationData":[OSD([sQuery(id+"F0.wireOp",EDGE,"E1.bottom")])],"isStart":false});
            fillet(context, id + "F15", {"entities" : qUnion([Q0]), "radius" : 2 * mm, "tangentPropagation" : true, "allowEdgeOverflow" : false});
        }
        {
            var Q0;
            {var subQ0=sQuery(id+"F0.wireOp",EDGE,"E21.filletArc");var subQ1=sQuery(id+"F0.wireOp",EDGE,"E7");var subQ2=sQuery(id+"F0.wireOp",EDGE,"E6");var subQ3=sQuery(id+"F0.wireOp",EDGE,"E5");var subQ4=sQuery(id+"F0.wireOp",EDGE,"E4");var subQ5=sQuery(id+"F0.wireOp",EDGE,"E22.filletArc");var subQ6=sQuery(id+"F0.wireOp",EDGE,"E1.bottom");var subQ7=sQuery(id+"F0.wireOp",EDGE,"E1.right");var subQ8=sQuery(id+"F0.wireOp",EDGE,"E1.top");var subQ9=sQuery(id+"F0.wireOp",EDGE,"E1.left");var subQ10=sQuery(id+"F0.wireOp",EDGE,"E23.filletArc");var subQ11=sQuery(id+"F0.wireOp",EDGE,"E24.filletArc");Q0=makeQuery(id+"F2.boolean.opBoolean","SPLIT",FACE,{"disambiguationData":[TD([makeQuery(id+"F1.opExtrude","SWEPT_FACE",FACE,{"disambiguationData":[OSD([subQ6])]})])],"derivedFrom":makeQuery(id+"F1.opExtrude","CAP_FACE",FACE,{"disambiguationData":[OSD([subQ6,subQ8,subQ9,subQ7,subQ4,subQ3,subQ2,subQ1,subQ0,subQ5,subQ10,subQ11])],"isStart":true})});}
            var sketch = newSketch(context, id + "F16", { "sketchPlane" : qUnion([Q0])});
            skLineSegment(sketch, "E79", {"start": v(0, 110) * mm, "end": v(0, 0) * mm, "construction": true});
            skArc(sketch, "E80", {"start": v(15, 110) * mm, "mid": v(0, 125.09) * mm, "end": v(-15, 110) * mm});
            skLineSegment(sketch, "E81", {"start": v(-15, 110) * mm, "end": v(-14.93, 98) * mm});
            skLineSegment(sketch, "E82", {"start": v(-14.93, 98) * mm, "end": v(-32.93, 80) * mm});
            skCircle(sketch, "E83", {"center": v(0, 110) * mm, "radius": 6 * mm});
            skLineSegment(sketch, "E84", {"start": v(15, 110) * mm, "end": v(15, 98) * mm});
            skLineSegment(sketch, "E85", {"start": v(15, 98) * mm, "end": v(33, 80) * mm});
            skLineSegment(sketch, "E86", {"start": v(-74.25, 0) * mm, "end": v(74.25, 0) * mm, "construction": true});
            skLineSegment(sketch, "E87.MirrorCS", {"start": v(15, -110) * mm, "end": v(15, -98) * mm});
            skCircle(sketch, "E88.MirrorC", {"center": v(0, -110) * mm, "radius": 6 * mm});
            skLineSegment(sketch, "E89.MirrorCS", {"start": v(-14.93, -98) * mm, "end": v(-32.93, -80) * mm});
            skLineSegment(sketch, "E90.MirrorCS", {"start": v(-15, -110) * mm, "end": v(-14.93, -98) * mm});
            skArc(sketch, "E91.MirrorCS", {"start": v(15, -110) * mm, "mid": v(0, -125.09) * mm, "end": v(-15, -110) * mm});
            skLineSegment(sketch, "E92.MirrorCS", {"start": v(15, -98) * mm, "end": v(33, -80) * mm});
            skSolve(sketch);
        }
        {
            var Q0;
            Q0=makeQuery(id+"F16.imprint","IMPRINT",FACE,{"disambiguationData":[TD([[makeQuery(id+"F16.imprint","IMPRINT",EDGE,{"derivedFrom":sQuery(id+"F16.wireOp",EDGE,"E80")}),1.0]])]});
            var Q1;
            Q1=makeQuery(id+"F16.imprint","IMPRINT",FACE,{"disambiguationData":[TD([[makeQuery(id+"F16.imprint","IMPRINT",EDGE,{"derivedFrom":sQuery(id+"F16.wireOp",EDGE,"E87.MirrorCS")}),1.0]])]});
            var Q2;
            Q2=makeQuery(id+"F16.imprint","IMPRINT",FACE,{"disambiguationData":[TD([[makeQuery(id+"F16.imprint","IMPRINT",EDGE,{"derivedFrom":makeQuery(id+"F1.opExtrude","CAP_EDGE",EDGE,{"disambiguationData":[OSD([sQuery(id+"F0.wireOp",EDGE,"E1.left")])],"isStart":true})}),-1.0]])]});
            var Q3;
            Q3=makeQuery(id+"F2.opExtrude","CAP_FACE",FACE,{"disambiguationData":[OSD([sQuery(id+"F0.wireOp",EDGE,"E12"),sQuery(id+"F0.wireOp",EDGE,"E13"),sQuery(id+"F0.wireOp",EDGE,"E14"),sQuery(id+"F0.wireOp",EDGE,"E15"),sQuery(id+"F0.wireOp",EDGE,"E17.filletArc"),sQuery(id+"F0.wireOp",EDGE,"E18.filletArc"),sQuery(id+"F0.wireOp",EDGE,"E19.filletArc"),sQuery(id+"F0.wireOp",EDGE,"E20.filletArc"),sQuery(id+"F0.wireOp",EDGE,"E25.0"),sQuery(id+"F0.wireOp",EDGE,"E25.1"),sQuery(id+"F0.wireOp",EDGE,"E25.2"),sQuery(id+"F0.wireOp",EDGE,"E25.3"),sQuery(id+"F0.wireOp",EDGE,"E25.4"),sQuery(id+"F0.wireOp",EDGE,"E25.5"),sQuery(id+"F0.wireOp",EDGE,"E25.6"),sQuery(id+"F0.wireOp",EDGE,"E25.7")])],"isStart":false});
            extrude(context, id + "F17", {"entities" : qUnion([Q0, Q1, Q2]), "endBound" : BoundingType.UP_TO_SURFACE, "endBoundEntityFace" : qUnion([Q3]), "depth" : 25 * mm});
        }
    });
